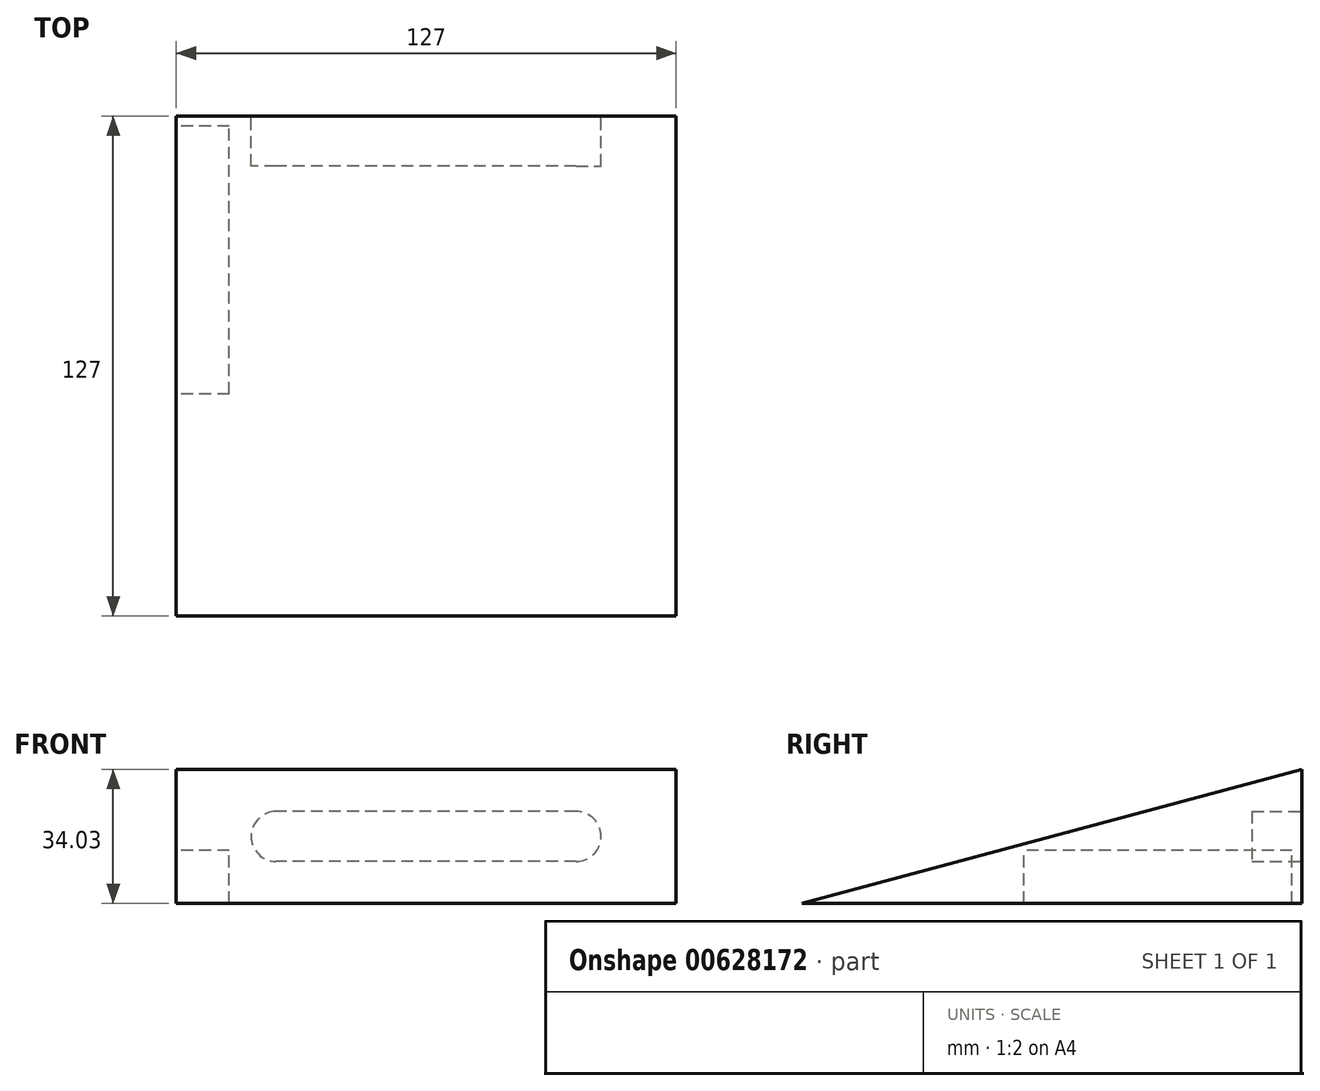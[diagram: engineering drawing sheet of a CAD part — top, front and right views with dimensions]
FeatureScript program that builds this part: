
annotation { "Feature Type Name" : "Feature", "Feature Type Description" : "" }
export const myFeature = defineFeature(function(context is Context, id is Id, definition is map)
    precondition{}
    {
        {
            var Q0;
            Q0=qCreatedBy(makeId("Right.planeOp"),FACE);
            var sketch = newSketch(context, id + "F0", { "sketchPlane" : qUnion([Q0])});
            skLineSegment(sketch, "E0", {"start": v(-66.49, 0) * mm, "end": v(60.51, 0) * mm});
            skLineSegment(sketch, "E1", {"start": v(-66.49, 0) * mm, "end": v(60.51, 34.03) * mm});
            skLineSegment(sketch, "E2", {"start": v(60.51, 0) * mm, "end": v(60.51, 34.03) * mm});
            skSolve(sketch);
        }
        {
            var Q0;
            Q0 = qSketchRegion(id + "F0", true);
            extrude(context, id + "F1", {"entities" : qUnion([Q0]), "depth" : 127 * mm, "offsetDistance" : 25.4 * mm});
        }
        {
            var Q0;
            Q0=makeQuery(id+"F1.opExtrude","CAP_FACE",FACE,{"disambiguationData":[OSD([sQuery(id+"F0.wireOp",EDGE,"E0"),sQuery(id+"F0.wireOp",EDGE,"E1"),sQuery(id+"F0.wireOp",EDGE,"E2")])],"isStart":true});
            var sketch = newSketch(context, id + "F2", { "sketchPlane" : qUnion([Q0])});
            skLineSegment(sketch, "E3.bottom", {"start": v(-57.97, 0) * mm, "end": v(10.1, 0) * mm});
            skLineSegment(sketch, "E3.top", {"start": v(-57.97, 13.46) * mm, "end": v(10.1, 13.46) * mm});
            skLineSegment(sketch, "E3.left", {"start": v(-57.97, 0) * mm, "end": v(-57.97, 13.46) * mm});
            skLineSegment(sketch, "E3.right", {"start": v(10.1, 0) * mm, "end": v(10.1, 13.46) * mm});
            skSolve(sketch);
        }
        {
            var Q0;
            Q0 = qSketchRegion(id + "F2", true);
            extrude(context, id + "F3", {"entities" : qUnion([Q0]), "operationType" : NewBodyOperationType.REMOVE, "oppositeDirection" : true, "depth" : 13.46 * mm, "offsetDistance" : 25.4 * mm});
        }
        {
            var Q0;
            Q0=makeQuery(id+"F1.opExtrude","SWEPT_FACE",FACE,{"disambiguationData":[OSD([sQuery(id+"F0.wireOp",EDGE,"E2")])]});
            var sketch = newSketch(context, id + "F4", { "sketchPlane" : qUnion([Q0])});
            skLineSegment(sketch, "E4", {"start": v(-127, 17.01) * mm, "end": v(-101.6, 17.01) * mm, "construction": true});
            skLineSegment(sketch, "E5", {"start": v(0, 17.01) * mm, "end": v(-25.4, 17.01) * mm, "construction": true});
            skLineSegment(sketch, "E6", {"start": v(-101.6, 17.01) * mm, "end": v(-25.4, 17.01) * mm, "construction": true});
            skArc(sketch, "E7.0.startCap", {"start": v(-101.6, 10.66) * mm, "mid": v(-107.95, 17.01) * mm, "end": v(-101.6, 23.36) * mm});
            skArc(sketch, "E7.0.endCap", {"start": v(-25.4, 23.36) * mm, "mid": v(-19.05, 17.01) * mm, "end": v(-25.4, 10.66) * mm});
            skLineSegment(sketch, "E7.0.left", {"start": v(-101.6, 23.36) * mm, "end": v(-25.4, 23.36) * mm});
            skLineSegment(sketch, "E7.0.right", {"start": v(-101.6, 10.66) * mm, "end": v(-25.4, 10.66) * mm});
            skSolve(sketch);
        }
        {
            var Q0;
            Q0 = qSketchRegion(id + "F4", true);
            extrude(context, id + "F5", {"entities" : qUnion([Q0]), "operationType" : NewBodyOperationType.REMOVE, "oppositeDirection" : true, "depth" : 12.7 * mm, "offsetDistance" : 25.4 * mm});
        }
    });
